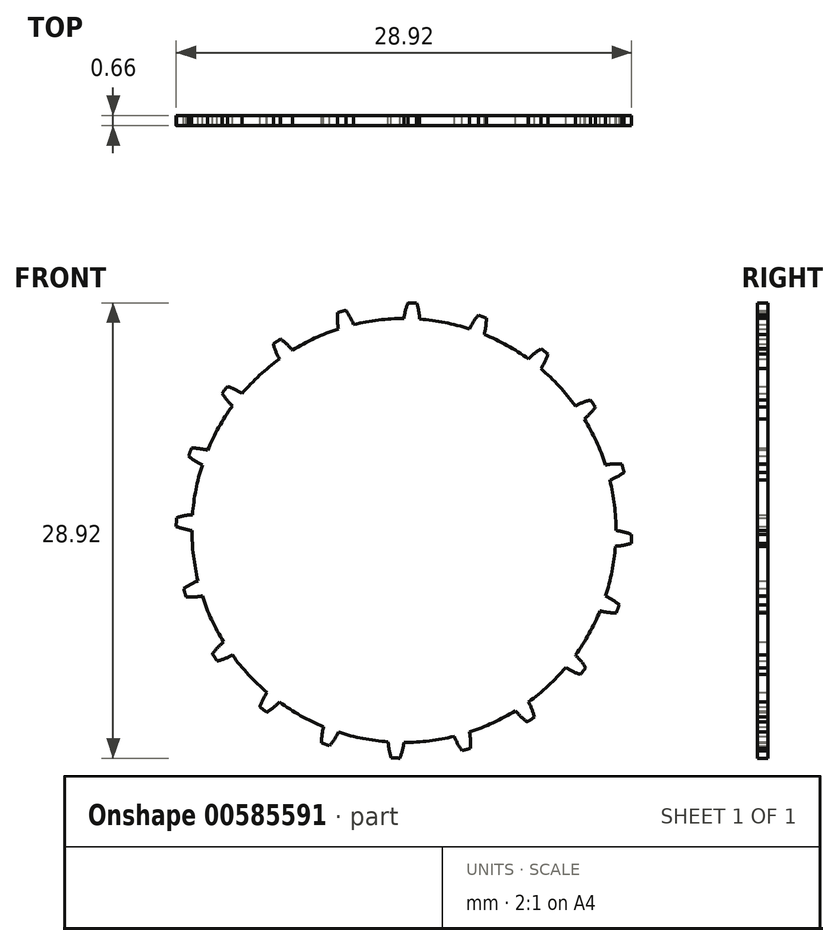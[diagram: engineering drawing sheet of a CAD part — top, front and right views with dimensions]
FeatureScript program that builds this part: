
annotation { "Feature Type Name" : "Feature", "Feature Type Description" : "" }
export const myFeature = defineFeature(function(context is Context, id is Id, definition is map)
    precondition{}
    {
        {
            var Q0;
            Q0=qCreatedBy(makeId("Front.planeOp"),FACE);
            var sketch = newSketch(context, id + "F0", { "sketchPlane" : qUnion([Q0])});
            skCircle(sketch, "E0", {"center": v(0, 0) * mm, "radius": 13.46 * mm});
            skCircle(sketch, "E1", {"center": v(0, 0) * mm, "radius": 14.46 * mm, "construction": true});
            skLineSegment(sketch, "E2", {"start": v(0, 0) * mm, "end": v(0, 17.12) * mm, "construction": true});
            skLineSegment(sketch, "E3.1.0", {"start": v(0, 0) * mm, "end": v(0.54, 17.1) * mm, "construction": true});
            skLineSegment(sketch, "E3.2.0", {"start": v(0, 0) * mm, "end": v(1.07, 17.08) * mm, "construction": true});
            skLineSegment(sketch, "E3.3.0", {"start": v(0, 0) * mm, "end": v(1.61, 17.04) * mm, "construction": true});
            skLineSegment(sketch, "E3.4.0", {"start": v(0, 0) * mm, "end": v(2.15, 16.98) * mm, "construction": true});
            skLineSegment(sketch, "E3.5.0", {"start": v(0, 0) * mm, "end": v(2.68, 16.9) * mm, "construction": true});
            skLineSegment(sketch, "E3.6.0", {"start": v(0, 0) * mm, "end": v(3.2, 16.81) * mm, "construction": true});
            skLineSegment(sketch, "E3.7.0", {"start": v(0, 0) * mm, "end": v(3.73, 16.7) * mm, "construction": true});
            skLineSegment(sketch, "E3.8.0", {"start": v(0, 0) * mm, "end": v(4.26, 16.58) * mm, "construction": true});
            skLineSegment(sketch, "E3.9.0", {"start": v(0, 0) * mm, "end": v(4.78, 16.44) * mm, "construction": true});
            skLineSegment(sketch, "E3.10.0", {"start": v(0, 0) * mm, "end": v(5.29, 16.28) * mm, "construction": true});
            skLineSegment(sketch, "E3.anchor2", {"start": v(0, 0) * mm, "end": v(5.29, 16.28) * mm, "construction": true});
            skPoint(sketch, "E4", {"position": v(0, 13.46) * mm});
            skPoint(sketch, "E5", {"position": v(0.42, 13.46) * mm});
            skPoint(sketch, "E6", {"position": v(0.85, 13.44) * mm});
            skPoint(sketch, "E7", {"position": v(1.27, 13.4) * mm});
            skPoint(sketch, "E8", {"position": v(1.69, 13.36) * mm});
            skPoint(sketch, "E9", {"position": v(2.1, 13.3) * mm});
            skPoint(sketch, "E10", {"position": v(2.52, 13.23) * mm});
            skPoint(sketch, "E11", {"position": v(2.94, 13.14) * mm});
            skPoint(sketch, "E12", {"position": v(3.35, 13.04) * mm});
            skPoint(sketch, "E13", {"position": v(3.76, 12.93) * mm});
            skPoint(sketch, "E14", {"position": v(4.16, 12.8) * mm});
            skLineSegment(sketch, "E15", {"start": v(0.42, 13.46) * mm, "end": v(0, 13.47) * mm});
            skPoint(sketch, "E16", {"position": v(0, 13.47) * mm});
            skLineSegment(sketch, "E17", {"start": v(0.85, 13.44) * mm, "end": v(0, 13.5) * mm});
            skPoint(sketch, "E18", {"position": v(0, 13.5) * mm});
            skLineSegment(sketch, "E19", {"start": v(1.27, 13.4) * mm, "end": v(0, 13.52) * mm});
            skPoint(sketch, "E20", {"position": v(0, 13.52) * mm});
            skLineSegment(sketch, "E21", {"start": v(1.69, 13.36) * mm, "end": v(0, 13.57) * mm});
            skLineSegment(sketch, "E22", {"start": v(2.1, 13.3) * mm, "end": v(0.02, 13.63) * mm});
            skLineSegment(sketch, "E23", {"start": v(2.52, 13.23) * mm, "end": v(0.03, 13.7) * mm});
            skLineSegment(sketch, "E24", {"start": v(2.94, 13.14) * mm, "end": v(0.05, 13.79) * mm});
            skLineSegment(sketch, "E25", {"start": v(3.35, 13.04) * mm, "end": v(0.07, 13.88) * mm});
            skLineSegment(sketch, "E26", {"start": v(3.76, 12.93) * mm, "end": v(0.1, 14) * mm});
            skLineSegment(sketch, "E27", {"start": v(4.16, 12.8) * mm, "end": v(0.14, 14.11) * mm});
            skPoint(sketch, "E28", {"position": v(0, 13.57) * mm});
            skPoint(sketch, "E29", {"position": v(0.02, 13.63) * mm});
            skPoint(sketch, "E30", {"position": v(0.03, 13.7) * mm});
            skPoint(sketch, "E31", {"position": v(0.05, 13.79) * mm});
            skPoint(sketch, "E32", {"position": v(0.07, 13.88) * mm});
            skPoint(sketch, "E33", {"position": v(0.1, 14) * mm});
            skPoint(sketch, "E34", {"position": v(0.14, 14.11) * mm});
            skLineSegment(sketch, "E35.1.0", {"start": v(0, 0) * mm, "end": v(6.3, 15.91) * mm, "construction": true});
            skLineSegment(sketch, "E35.2.0", {"start": v(0, 0) * mm, "end": v(7.29, 15.49) * mm, "construction": true});
            skLineSegment(sketch, "E35.3.0", {"start": v(0, 0) * mm, "end": v(8.25, 15) * mm, "construction": true});
            skLineSegment(sketch, "E35.4.0", {"start": v(0, 0) * mm, "end": v(9.17, 14.45) * mm, "construction": true});
            skLineSegment(sketch, "E35.5.0", {"start": v(0, 0) * mm, "end": v(10.06, 13.85) * mm, "construction": true});
            skLineSegment(sketch, "E35.anchor2", {"start": v(0, 0) * mm, "end": v(10.06, 13.85) * mm, "construction": true});
            skPoint(sketch, "E36", {"position": v(4.96, 12.52) * mm});
            skPoint(sketch, "E37", {"position": v(5.73, 12.18) * mm});
            skPoint(sketch, "E38", {"position": v(6.49, 11.8) * mm});
            skLineSegment(sketch, "E39", {"start": v(4.96, 12.52) * mm, "end": v(0.24, 14.39) * mm});
            skPoint(sketch, "E40", {"position": v(0.24, 14.39) * mm});
            skLineSegment(sketch, "E41", {"start": v(5.73, 12.18) * mm, "end": v(0.37, 14.7) * mm});
            skPoint(sketch, "E42", {"position": v(0.37, 14.7) * mm});
            skCircle(sketch, "E43.converted", {"center": v(3.8, 13) * mm, "radius": 3.83 * mm});
            skSolve(sketch);
        }
        {
            var Q0;
            Q0=qCreatedBy(makeId("Front.planeOp"),FACE);
            var sketch = newSketch(context, id + "F1", { "sketchPlane" : qUnion([Q0])});
            skCircle(sketch, "E44.0", {"center": v(0, 0) * mm, "radius": 13.46 * mm});
            skCircle(sketch, "E45.0", {"center": v(0, 0) * mm, "radius": 14.46 * mm, "construction": true});
            skCircle(sketch, "E46.62", {"center": v(3.8, 13) * mm, "radius": 3.83 * mm, "construction": true});
            skLineSegment(sketch, "E47", {"start": v(0, 0) * mm, "end": v(1.33, 18.02) * mm, "construction": true});
            skLineSegment(sketch, "E48", {"start": v(0, 0) * mm, "end": v(0.65, 17.45) * mm, "construction": true});
            skLineSegment(sketch, "E49", {"start": v(0, 0) * mm, "end": v(1.68, 19.85) * mm, "construction": true});
            skSolve(sketch);
        }
        {
            var Q0;
            Q0=qCreatedBy(makeId("Front.planeOp"),FACE);
            var sketch = newSketch(context, id + "F2", { "sketchPlane" : qUnion([Q0])});
            skCircle(sketch, "E50.0", {"center": v(0, 0) * mm, "radius": 13.46 * mm});
            skArc(sketch, "E51.0", {"start": v(0.81, 14.44) * mm, "mid": v(0.54, 14.45) * mm, "end": v(0.26, 14.46) * mm});
            skLineSegment(sketch, "E52.0", {"start": v(0, 0) * mm, "end": v(0.65, 17.45) * mm, "construction": true});
            skArc(sketch, "E53.0", {"start": v(0.26, 14.46) * mm, "mid": v(0.1, 13.97) * mm, "end": v(0, 13.46) * mm});
            skArc(sketch, "E54.MirrorCS", {"start": v(0.81, 14.44) * mm, "mid": v(0.94, 13.94) * mm, "end": v(1, 13.43) * mm});
            skArc(sketch, "E55.1.0", {"start": v(-4.22, 13.84) * mm, "mid": v(-4.22, 13.32) * mm, "end": v(-4.16, 12.8) * mm});
            skArc(sketch, "E55.1.1", {"start": v(-3.7, 13.99) * mm, "mid": v(-3.96, 13.91) * mm, "end": v(-4.22, 13.84) * mm});
            skArc(sketch, "E55.1.2", {"start": v(-3.7, 13.99) * mm, "mid": v(-3.41, 13.55) * mm, "end": v(-3.2, 13.08) * mm});
            skArc(sketch, "E55.2.0", {"start": v(-8.29, 11.86) * mm, "mid": v(-8.13, 11.36) * mm, "end": v(-7.91, 10.9) * mm});
            skArc(sketch, "E55.2.1", {"start": v(-7.83, 12.16) * mm, "mid": v(-8.06, 12) * mm, "end": v(-8.29, 11.86) * mm});
            skArc(sketch, "E55.2.2", {"start": v(-7.83, 12.16) * mm, "mid": v(-7.43, 11.83) * mm, "end": v(-7.08, 11.45) * mm});
            skArc(sketch, "E55.3.0", {"start": v(-11.55, 8.71) * mm, "mid": v(-11.25, 8.3) * mm, "end": v(-10.9, 7.91) * mm});
            skArc(sketch, "E55.3.1", {"start": v(-11.2, 9.14) * mm, "mid": v(-11.38, 8.93) * mm, "end": v(-11.55, 8.71) * mm});
            skArc(sketch, "E55.3.2", {"start": v(-11.2, 9.14) * mm, "mid": v(-10.73, 8.95) * mm, "end": v(-10.28, 8.7) * mm});
            skArc(sketch, "E55.4.0", {"start": v(-13.67, 4.72) * mm, "mid": v(-13.26, 4.41) * mm, "end": v(-12.8, 4.16) * mm});
            skArc(sketch, "E55.4.1", {"start": v(-13.48, 5.23) * mm, "mid": v(-13.58, 4.98) * mm, "end": v(-13.67, 4.72) * mm});
            skArc(sketch, "E55.4.2", {"start": v(-13.48, 5.23) * mm, "mid": v(-12.97, 5.2) * mm, "end": v(-12.46, 5.1) * mm});
            skArc(sketch, "E55.5.0", {"start": v(-14.46, 0.26) * mm, "mid": v(-13.97, 0.1) * mm, "end": v(-13.46, 0) * mm});
            skArc(sketch, "E55.5.1", {"start": v(-14.44, 0.81) * mm, "mid": v(-14.45, 0.54) * mm, "end": v(-14.46, 0.26) * mm});
            skArc(sketch, "E55.5.2", {"start": v(-14.44, 0.81) * mm, "mid": v(-13.94, 0.94) * mm, "end": v(-13.43, 1) * mm});
            skArc(sketch, "E55.6.0", {"start": v(-13.84, -4.22) * mm, "mid": v(-13.32, -4.22) * mm, "end": v(-12.8, -4.16) * mm});
            skArc(sketch, "E55.6.1", {"start": v(-13.99, -3.7) * mm, "mid": v(-13.91, -3.96) * mm, "end": v(-13.84, -4.22) * mm});
            skArc(sketch, "E55.6.2", {"start": v(-13.99, -3.7) * mm, "mid": v(-13.55, -3.41) * mm, "end": v(-13.08, -3.2) * mm});
            skArc(sketch, "E55.7.0", {"start": v(-11.86, -8.29) * mm, "mid": v(-11.36, -8.13) * mm, "end": v(-10.9, -7.91) * mm});
            skArc(sketch, "E55.7.1", {"start": v(-12.16, -7.83) * mm, "mid": v(-12, -8.06) * mm, "end": v(-11.86, -8.29) * mm});
            skArc(sketch, "E55.7.2", {"start": v(-12.16, -7.83) * mm, "mid": v(-11.83, -7.43) * mm, "end": v(-11.45, -7.08) * mm});
            skArc(sketch, "E55.8.0", {"start": v(-8.71, -11.55) * mm, "mid": v(-8.3, -11.25) * mm, "end": v(-7.91, -10.9) * mm});
            skArc(sketch, "E55.8.1", {"start": v(-9.14, -11.2) * mm, "mid": v(-8.93, -11.38) * mm, "end": v(-8.71, -11.55) * mm});
            skArc(sketch, "E55.8.2", {"start": v(-9.14, -11.2) * mm, "mid": v(-8.95, -10.73) * mm, "end": v(-8.7, -10.28) * mm});
            skArc(sketch, "E55.9.0", {"start": v(-4.72, -13.67) * mm, "mid": v(-4.41, -13.26) * mm, "end": v(-4.16, -12.8) * mm});
            skArc(sketch, "E55.9.1", {"start": v(-5.23, -13.48) * mm, "mid": v(-4.98, -13.58) * mm, "end": v(-4.72, -13.67) * mm});
            skArc(sketch, "E55.9.2", {"start": v(-5.23, -13.48) * mm, "mid": v(-5.2, -12.97) * mm, "end": v(-5.1, -12.46) * mm});
            skArc(sketch, "E55.10.0", {"start": v(-0.26, -14.46) * mm, "mid": v(-0.1, -13.97) * mm, "end": v(0, -13.46) * mm});
            skArc(sketch, "E55.10.1", {"start": v(-0.81, -14.44) * mm, "mid": v(-0.54, -14.45) * mm, "end": v(-0.26, -14.46) * mm});
            skArc(sketch, "E55.10.2", {"start": v(-0.81, -14.44) * mm, "mid": v(-0.94, -13.94) * mm, "end": v(-1, -13.43) * mm});
            skArc(sketch, "E55.11.0", {"start": v(4.22, -13.84) * mm, "mid": v(4.22, -13.32) * mm, "end": v(4.16, -12.8) * mm});
            skArc(sketch, "E55.11.1", {"start": v(3.7, -13.99) * mm, "mid": v(3.96, -13.91) * mm, "end": v(4.22, -13.84) * mm});
            skArc(sketch, "E55.11.2", {"start": v(3.7, -13.99) * mm, "mid": v(3.41, -13.55) * mm, "end": v(3.2, -13.08) * mm});
            skArc(sketch, "E55.12.0", {"start": v(8.29, -11.86) * mm, "mid": v(8.13, -11.36) * mm, "end": v(7.91, -10.9) * mm});
            skArc(sketch, "E55.12.1", {"start": v(7.83, -12.16) * mm, "mid": v(8.06, -12) * mm, "end": v(8.29, -11.86) * mm});
            skArc(sketch, "E55.12.2", {"start": v(7.83, -12.16) * mm, "mid": v(7.43, -11.83) * mm, "end": v(7.08, -11.45) * mm});
            skArc(sketch, "E55.13.0", {"start": v(11.55, -8.71) * mm, "mid": v(11.25, -8.3) * mm, "end": v(10.9, -7.91) * mm});
            skArc(sketch, "E55.13.1", {"start": v(11.2, -9.14) * mm, "mid": v(11.38, -8.93) * mm, "end": v(11.55, -8.71) * mm});
            skArc(sketch, "E55.13.2", {"start": v(11.2, -9.14) * mm, "mid": v(10.73, -8.95) * mm, "end": v(10.28, -8.7) * mm});
            skArc(sketch, "E55.14.0", {"start": v(13.67, -4.72) * mm, "mid": v(13.26, -4.41) * mm, "end": v(12.8, -4.16) * mm});
            skArc(sketch, "E55.14.1", {"start": v(13.48, -5.23) * mm, "mid": v(13.58, -4.98) * mm, "end": v(13.67, -4.72) * mm});
            skArc(sketch, "E55.14.2", {"start": v(13.48, -5.23) * mm, "mid": v(12.97, -5.2) * mm, "end": v(12.46, -5.1) * mm});
            skArc(sketch, "E55.15.0", {"start": v(14.46, -0.26) * mm, "mid": v(13.97, -0.1) * mm, "end": v(13.46, 0) * mm});
            skArc(sketch, "E55.15.1", {"start": v(14.44, -0.81) * mm, "mid": v(14.45, -0.54) * mm, "end": v(14.46, -0.26) * mm});
            skArc(sketch, "E55.15.2", {"start": v(14.44, -0.81) * mm, "mid": v(13.94, -0.94) * mm, "end": v(13.43, -1) * mm});
            skArc(sketch, "E55.16.0", {"start": v(13.84, 4.22) * mm, "mid": v(13.32, 4.22) * mm, "end": v(12.8, 4.16) * mm});
            skArc(sketch, "E55.16.1", {"start": v(13.99, 3.7) * mm, "mid": v(13.91, 3.96) * mm, "end": v(13.84, 4.22) * mm});
            skArc(sketch, "E55.16.2", {"start": v(13.99, 3.7) * mm, "mid": v(13.55, 3.41) * mm, "end": v(13.08, 3.2) * mm});
            skArc(sketch, "E55.17.0", {"start": v(11.86, 8.29) * mm, "mid": v(11.36, 8.13) * mm, "end": v(10.9, 7.91) * mm});
            skArc(sketch, "E55.17.1", {"start": v(12.16, 7.83) * mm, "mid": v(12, 8.06) * mm, "end": v(11.86, 8.29) * mm});
            skArc(sketch, "E55.17.2", {"start": v(12.16, 7.83) * mm, "mid": v(11.83, 7.43) * mm, "end": v(11.45, 7.08) * mm});
            skArc(sketch, "E55.18.0", {"start": v(8.71, 11.55) * mm, "mid": v(8.3, 11.25) * mm, "end": v(7.91, 10.9) * mm});
            skArc(sketch, "E55.18.1", {"start": v(9.14, 11.2) * mm, "mid": v(8.93, 11.38) * mm, "end": v(8.71, 11.55) * mm});
            skArc(sketch, "E55.18.2", {"start": v(9.14, 11.2) * mm, "mid": v(8.95, 10.73) * mm, "end": v(8.7, 10.28) * mm});
            skArc(sketch, "E55.19.0", {"start": v(4.72, 13.67) * mm, "mid": v(4.41, 13.26) * mm, "end": v(4.16, 12.8) * mm});
            skArc(sketch, "E55.19.1", {"start": v(5.23, 13.48) * mm, "mid": v(4.98, 13.58) * mm, "end": v(4.72, 13.67) * mm});
            skArc(sketch, "E55.19.2", {"start": v(5.23, 13.48) * mm, "mid": v(5.2, 12.97) * mm, "end": v(5.1, 12.46) * mm});
            skSolve(sketch);
        }
        {
            var Q0;
            Q0 = qSketchRegion(id + "F2", true);
            extrude(context, id + "F3", {"entities" : qUnion([Q0]), "depth" : 0.33 * mm, "offsetDistance" : 25 * mm, "hasSecondDirection" : true, "secondDirectionOppositeDirection" : true, "secondDirectionDepth" : 0.33 * mm});
        }
    });
